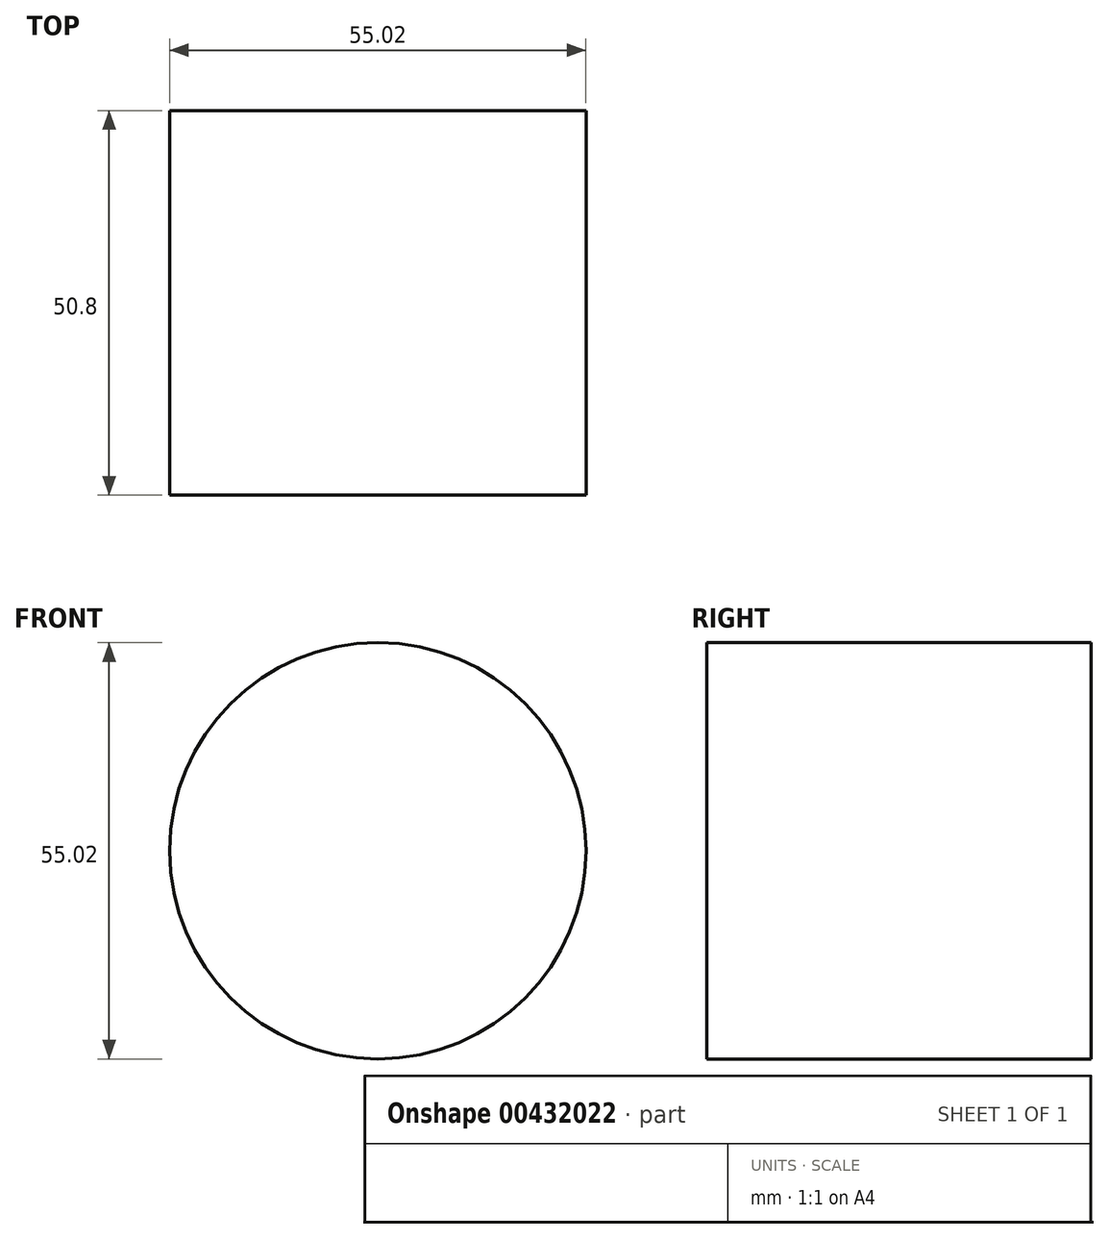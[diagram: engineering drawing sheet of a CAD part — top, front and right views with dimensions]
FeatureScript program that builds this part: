
annotation { "Feature Type Name" : "Feature", "Feature Type Description" : "" }
export const myFeature = defineFeature(function(context is Context, id is Id, definition is map)
    precondition{}
    {
        {
            var Q0;
            Q0=qCreatedBy(makeId("Front.planeOp"),FACE);
            var sketch = newSketch(context, id + "F0", { "sketchPlane" : qUnion([Q0])});
            skCircle(sketch, "E0", {"center": v(0, 0) * mm, "radius": 27.51 * mm});
            skSolve(sketch);
        }
        {
            var Q0;
            Q0 = qSketchRegion(id + "F0", true);
            extrude(context, id + "F1", {"entities" : qUnion([Q0]), "endBound" : BoundingType.SYMMETRIC, "depth" : 50.8 * mm});
        }
    });
